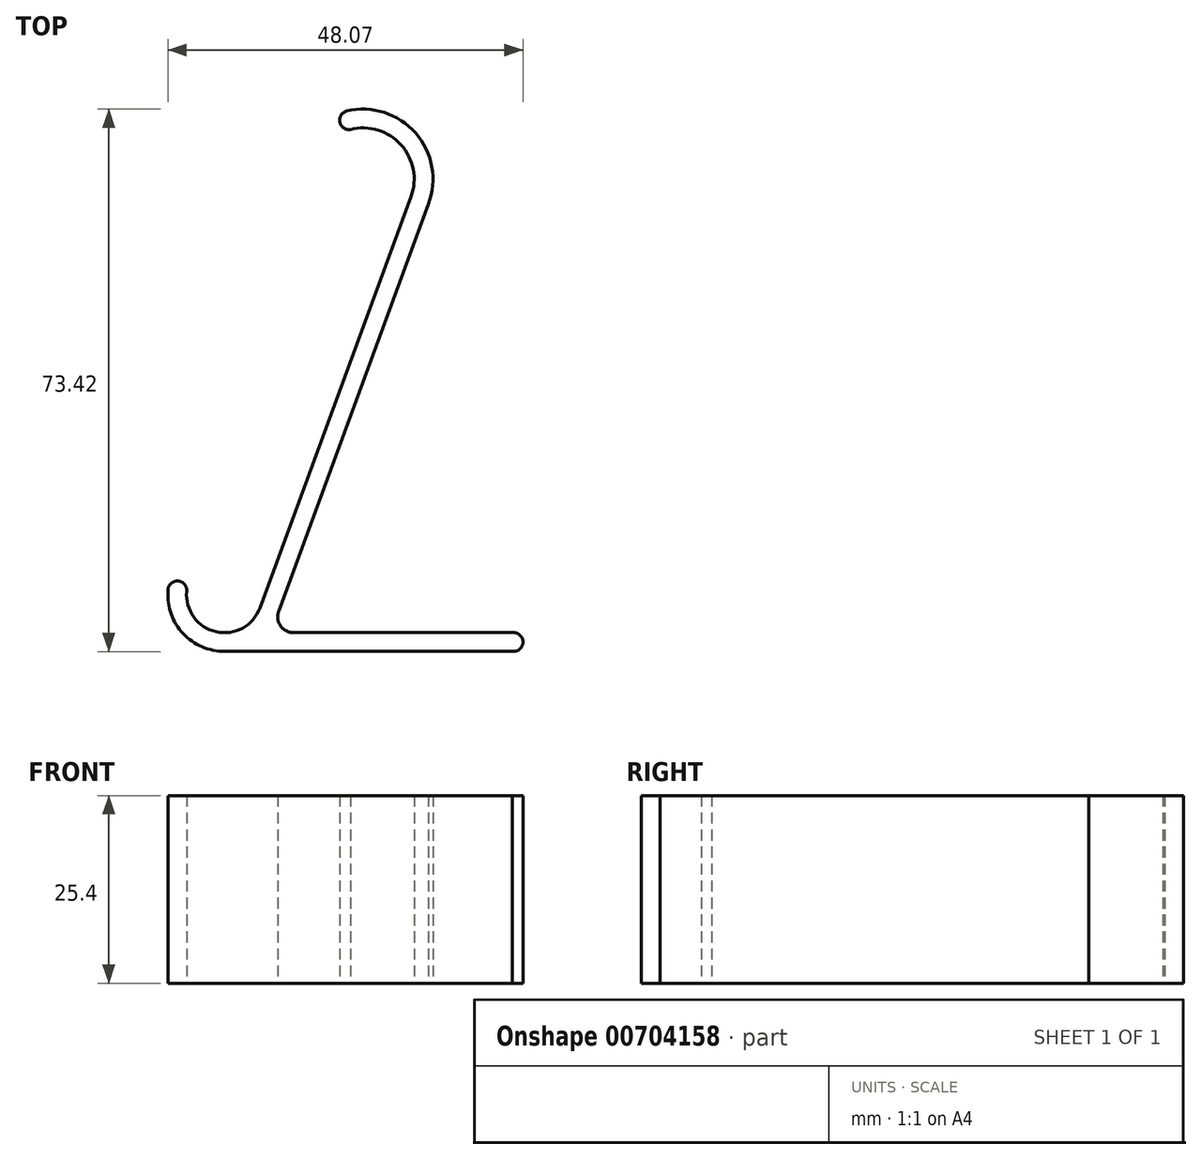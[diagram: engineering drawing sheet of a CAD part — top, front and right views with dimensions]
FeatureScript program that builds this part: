
annotation { "Feature Type Name" : "Feature", "Feature Type Description" : "" }
export const myFeature = defineFeature(function(context is Context, id is Id, definition is map)
    precondition{}
    {
        {
            var Q0;
            Q0=qCreatedBy(makeId("Top.planeOp"),FACE);
            var sketch = newSketch(context, id + "F0", { "sketchPlane" : qUnion([Q0])});
            skLineSegment(sketch, "E0", {"start": v(-40.28, 5.47) * mm, "end": v(-1.3, 5.47) * mm});
            skLineSegment(sketch, "E1", {"start": v(-1.13, 8.01) * mm, "end": v(-30.93, 8.01) * mm});
            skLineSegment(sketch, "E2", {"start": v(-32.94, 10.89) * mm, "end": v(-12.67, 66.03) * mm});
            skLineSegment(sketch, "E3", {"start": v(-15.01, 67) * mm, "end": v(-35.47, 11.36) * mm});
            skArc(sketch, "E4", {"start": v(-35.47, 11.36) * mm, "mid": v(-41.4, 8.13) * mm, "end": v(-45.38, 13.6) * mm});
            skArc(sketch, "E5", {"start": v(-40.28, 5.47) * mm, "mid": v(-45.86, 7.89) * mm, "end": v(-47.92, 13.6) * mm});
            skArc(sketch, "E6", {"start": v(-45.38, 13.6) * mm, "mid": v(-46.65, 15) * mm, "end": v(-47.92, 13.6) * mm});
            skArc(sketch, "E7.filletArc", {"start": v(-32.94, 10.89) * mm, "mid": v(-32.69, 8.93) * mm, "end": v(-30.93, 8.01) * mm});
            skArc(sketch, "E8", {"start": v(-15.01, 67) * mm, "mid": v(-16.37, 74.04) * mm, "end": v(-23.22, 76.13) * mm});
            skArc(sketch, "E9", {"start": v(-12.67, 66.03) * mm, "mid": v(-14.4, 75.65) * mm, "end": v(-23.7, 78.62) * mm});
            skArc(sketch, "E10", {"start": v(-1.13, 8.01) * mm, "mid": v(0.14, 6.65) * mm, "end": v(-1.3, 5.47) * mm});
            skArc(sketch, "E11", {"start": v(-23.7, 78.62) * mm, "mid": v(-24.66, 77.14) * mm, "end": v(-23.22, 76.13) * mm});
            skSolve(sketch);
        }
        {
            var Q0;
            Q0=makeQuery(id+"F0.imprint","IMPRINT",FACE,{"disambiguationData":[TD([[makeQuery(id+"F0.imprint","IMPRINT",EDGE,{"derivedFrom":sQuery(id+"F0.wireOp",EDGE,"E0")}),1.0]])]});
            extrude(context, id + "F1", {"entities" : qUnion([Q0]), "depth" : 25.4 * mm, "offsetDistance" : 25.4 * mm});
        }
    });
